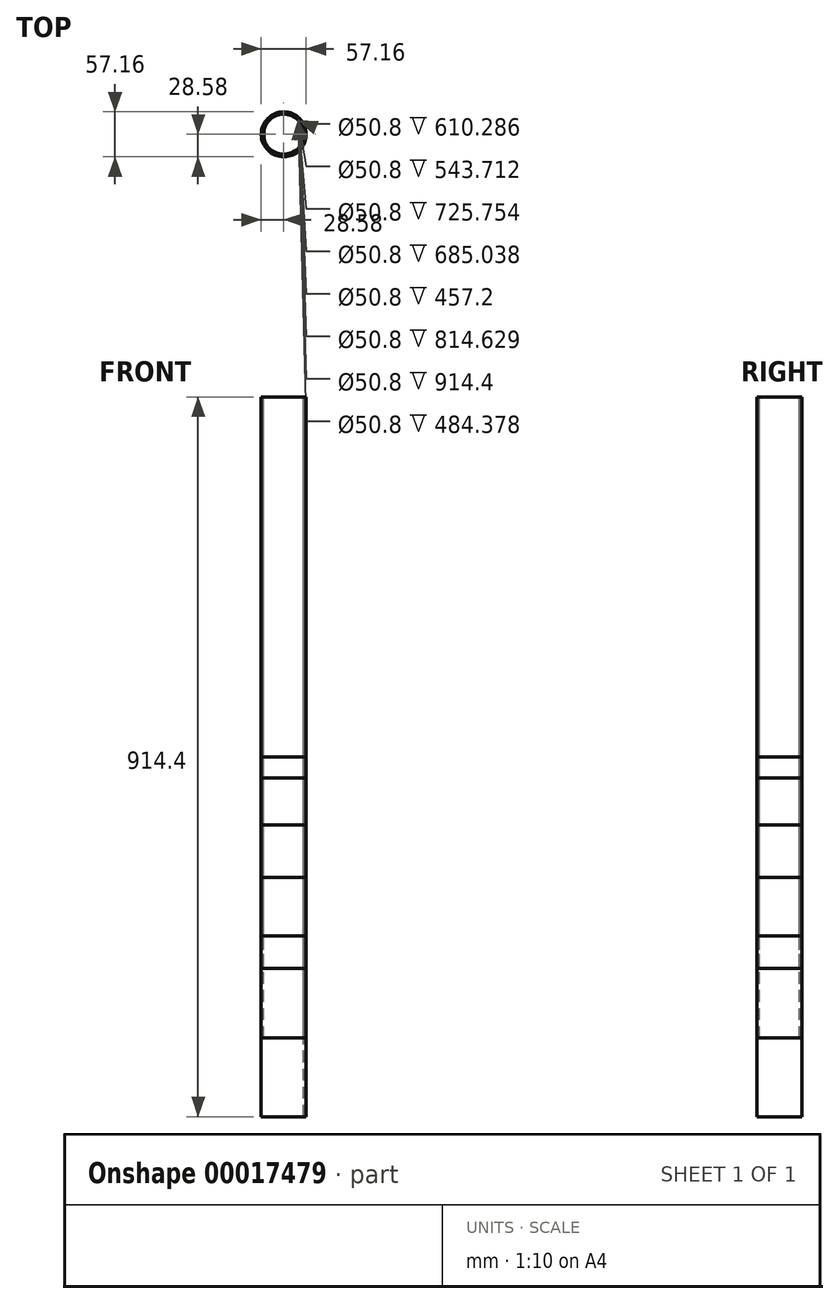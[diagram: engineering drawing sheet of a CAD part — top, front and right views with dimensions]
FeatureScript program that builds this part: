
annotation { "Feature Type Name" : "Feature", "Feature Type Description" : "" }
export const myFeature = defineFeature(function(context is Context, id is Id, definition is map)
    precondition{}
    {
        {
            var Q0;
            Q0=qCreatedBy(makeId("Top.planeOp"),FACE);
            var sketch = newSketch(context, id + "F0", { "sketchPlane" : qUnion([Q0])});
            skCircle(sketch, "E0", {"center": v(0, 0) * mm, "radius": 25.4 * mm});
            skCircle(sketch, "E1", {"center": v(0, 0) * mm, "radius": 28.58 * mm});
            skSolve(sketch);
        }
        {
            var Q0;
            Q0=makeQuery(id+"F0.imprint","IMPRINT",FACE,{"disambiguationData":[TD([[makeQuery(id+"F0.imprint","IMPRINT",EDGE,{"derivedFrom":sQuery(id+"F0.wireOp",EDGE,"E0")}),-1.0]])]});
            extrude(context, id + "F1", {"entities" : qUnion([Q0]), "oppositeDirection" : true, "depth" : 914.4 * mm});
        }
        {
            var Q0;
            Q0=makeQuery(id+"F1.opExtrude","CAP_FACE",FACE,{"disambiguationData":[OSD([sQuery(id+"F0.wireOp",EDGE,"E0"),sQuery(id+"F0.wireOp",EDGE,"E1")])],"isStart":true});
            extrude(context, id + "F2", {"entities" : qUnion([Q0]), "oppositeDirection" : true, "depth" : 457.2 * mm});
        }
        {
            var Q0;
            Q0 = qSketchRegion(id + "F0", true);
            extrude(context, id + "F3", {"entities" : qUnion([Q0]), "oppositeDirection" : true, "depth" : 814.63 * mm});
        }
        {
            var Q0;
            Q0 = qSketchRegion(id + "F0", true);
            extrude(context, id + "F4", {"entities" : qUnion([Q0]), "oppositeDirection" : true, "depth" : 725.75 * mm});
        }
        {
            var Q0;
            Q0 = qSketchRegion(id + "F0", true);
            extrude(context, id + "F5", {"entities" : qUnion([Q0]), "oppositeDirection" : true, "depth" : 685.04 * mm});
        }
        {
            var Q0;
            Q0 = qSketchRegion(id + "F0", true);
            extrude(context, id + "F6", {"entities" : qUnion([Q0]), "oppositeDirection" : true, "depth" : 610.3 * mm});
        }
        {
            var Q0;
            Q0 = qSketchRegion(id + "F0", true);
            extrude(context, id + "F7", {"entities" : qUnion([Q0]), "oppositeDirection" : true, "depth" : 543.7 * mm});
        }
        {
            var Q0;
            Q0 = qSketchRegion(id + "F0", true);
            extrude(context, id + "F8", {"entities" : qUnion([Q0]), "oppositeDirection" : true, "depth" : 484.38 * mm});
        }
    });
